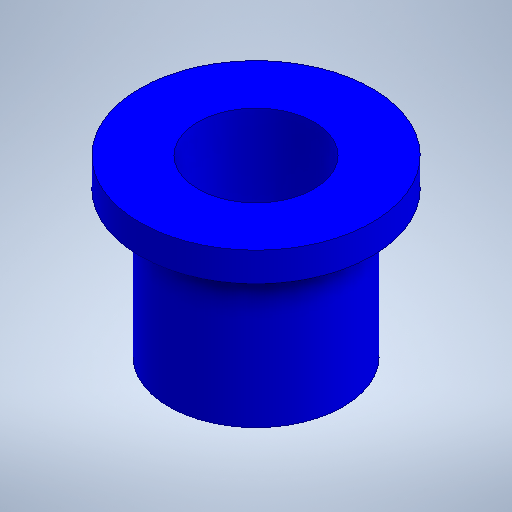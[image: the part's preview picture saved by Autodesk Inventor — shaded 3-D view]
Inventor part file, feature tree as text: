
AUTODESK INVENTOR PART (.ipt)
format: ipt  version: 2025.2 (Build 292293000, 293)  size: 221,184 bytes
history: native  units: mm
features: extrude x2, sketch x2
ambient origin geometry x8: Origin, YZ Plane, XZ Plane, XY Plane, X Axis, Y Axis, Z Axis, Center Point
bodies: Solid1 (feature_tree)
feature tree (4):
  extrude  "Extrusion1"  Depth=40.0mm
  extrude  "Extrusion2"  Depth=40.0mm
  sketch  "Sketch1"  dims[d0=80.0mm d1=40.0mm]
  sketch  "Sketch2"  dims[d2=10.0mm d3=0.0mm d4=40.0mm d5=60.0mm d6=50.0mm d7=0.0mm]
